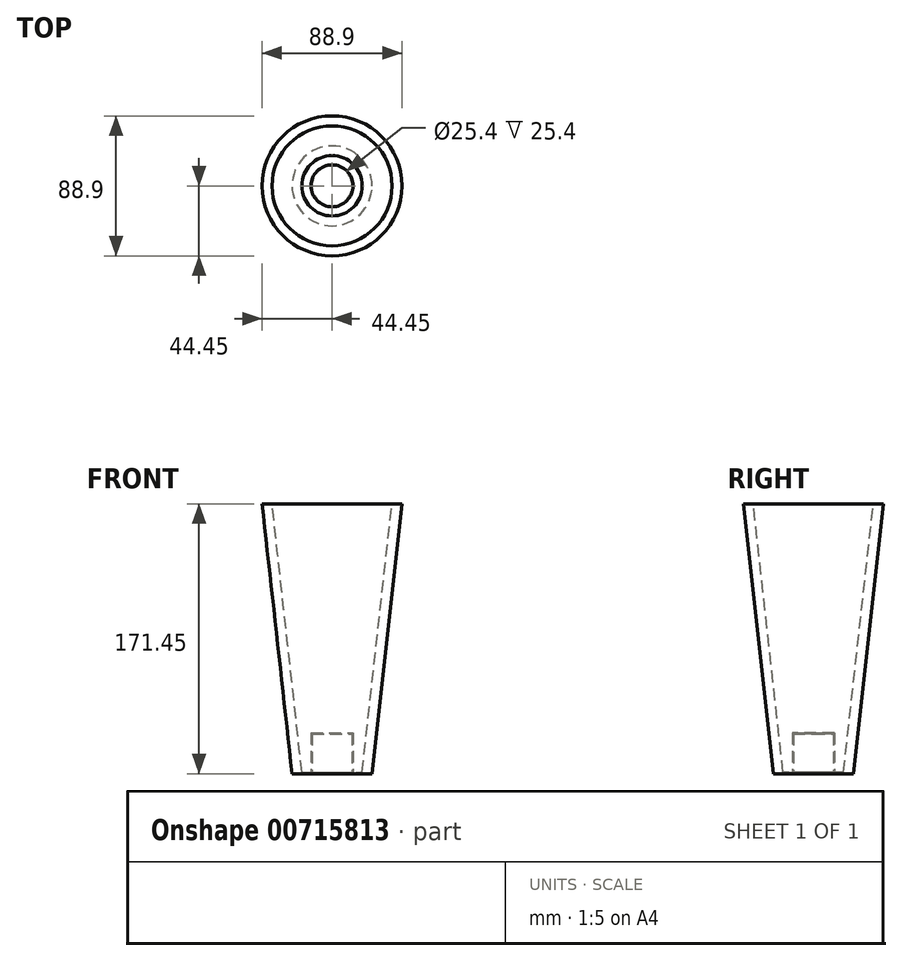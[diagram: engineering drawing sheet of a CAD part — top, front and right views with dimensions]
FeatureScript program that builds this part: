
annotation { "Feature Type Name" : "Feature", "Feature Type Description" : "" }
export const myFeature = defineFeature(function(context is Context, id is Id, definition is map)
    precondition{}
    {
        {
            var Q0;
            Q0=qCreatedBy(makeId("Front.planeOp"),FACE);
            var sketch = newSketch(context, id + "F0", { "sketchPlane" : qUnion([Q0])});
            skLineSegment(sketch, "E0", {"start": v(0, 77.15) * mm, "end": v(-44.45, 77.15) * mm});
            skLineSegment(sketch, "E1", {"start": v(-25.4, -94.3) * mm, "end": v(-44.45, 77.15) * mm});
            skLineSegment(sketch, "E2", {"start": v(-25.4, -94.3) * mm, "end": v(-12.7, -94.3) * mm});
            skLineSegment(sketch, "E3", {"start": v(-12.7, -94.3) * mm, "end": v(-12.7, -68.9) * mm});
            skLineSegment(sketch, "E4", {"start": v(-12.7, -68.9) * mm, "end": v(0, -68.9) * mm});
            skLineSegment(sketch, "E5", {"start": v(0, -68.9) * mm, "end": v(0, 77.15) * mm});
            skLineSegment(sketch, "E6", {"start": v(-38.1, 77.15) * mm, "end": v(-19.05, -94.3) * mm});
            skLineSegment(sketch, "E7", {"start": v(-25.5, -93.36) * mm, "end": v(-12.7, -93.36) * mm});
            skLineSegment(sketch, "E8", {"start": v(0, -68.26) * mm, "end": v(-13.33, -68.26) * mm});
            skLineSegment(sketch, "E9", {"start": v(-13.33, -68.26) * mm, "end": v(-13.33, -94.3) * mm});
            skSolve(sketch);
        }
        {
            var Q0;
            {var subQ0=sQuery(id+"F0.wireOp",EDGE,"E2");var subQ1=sQuery(id+"F0.wireOp",EDGE,"E1");var subQ2=makeQuery(id+"F0.imprint","INTERSECT",VERTEX,{"derivedFrom":[subQ1,subQ0]});Q0=makeQuery(id+"F0.imprint","IMPRINT",FACE,{"disambiguationData":[TD([[makeQuery(id+"F0.imprint","IMPRINT",EDGE,{"disambiguationData":[TD([[subQ2,-1.0]])],"derivedFrom":subQ1}),-1.0]])]});}
            var Q1;
            {var subQ0=sQuery(id+"F0.wireOp",EDGE,"E3");var subQ1=sQuery(id+"F0.wireOp",EDGE,"E2");var subQ2=makeQuery(id+"F0.imprint","INTERSECT",VERTEX,{"derivedFrom":[subQ1,subQ0]});Q1=makeQuery(id+"F0.imprint","IMPRINT",FACE,{"disambiguationData":[TD([[makeQuery(id+"F0.imprint","IMPRINT",EDGE,{"disambiguationData":[TD([[subQ2,1.0]])],"derivedFrom":subQ1}),1.0]])]});}
            var Q2;
            {var subQ6=sQuery(id+"F0.wireOp",EDGE,"E4");Q2=makeQuery(id+"F0.imprint","IMPRINT",FACE,{"disambiguationData":[TD([[makeQuery(id+"F0.imprint","IMPRINT",EDGE,{"derivedFrom":subQ6}),1.0]])]});}
            var Q3;
            {var subQ0=sQuery(id+"F0.wireOp",EDGE,"E6");var subQ1=sQuery(id+"F0.wireOp",EDGE,"E2");var subQ2=makeQuery(id+"F0.imprint","INTERSECT",VERTEX,{"derivedFrom":[subQ1,subQ0]});Q3=makeQuery(id+"F0.imprint","IMPRINT",FACE,{"disambiguationData":[TD([[makeQuery(id+"F0.imprint","IMPRINT",EDGE,{"disambiguationData":[TD([[subQ2,-1.0]])],"derivedFrom":subQ1}),1.0]])]});}
            var Q4;
            {var subQ0=sQuery(id+"F0.wireOp",EDGE,"E1");var subQ1=sQuery(id+"F0.wireOp",EDGE,"E0");var subQ2=makeQuery(id+"F0.imprint","INTERSECT",VERTEX,{"derivedFrom":[subQ1,subQ0]});Q4=makeQuery(id+"F0.imprint","IMPRINT",FACE,{"disambiguationData":[TD([[makeQuery(id+"F0.imprint","IMPRINT",EDGE,{"disambiguationData":[TD([[subQ2,1.0]])],"derivedFrom":subQ1}),1.0]])]});}
            var Q5;
            Q5=sQuery(id+"F0.wireOp",EDGE,"E5");
            revolve(context, id + "F1", {"surfaceOperationType" : NewSurfaceOperationType.NEW, "entities" : qUnion([Q0, Q1, Q2, Q3, Q4]), "axis" : qUnion([Q5]), "revolveType" : RevolveType.FULL});
        }
    });
